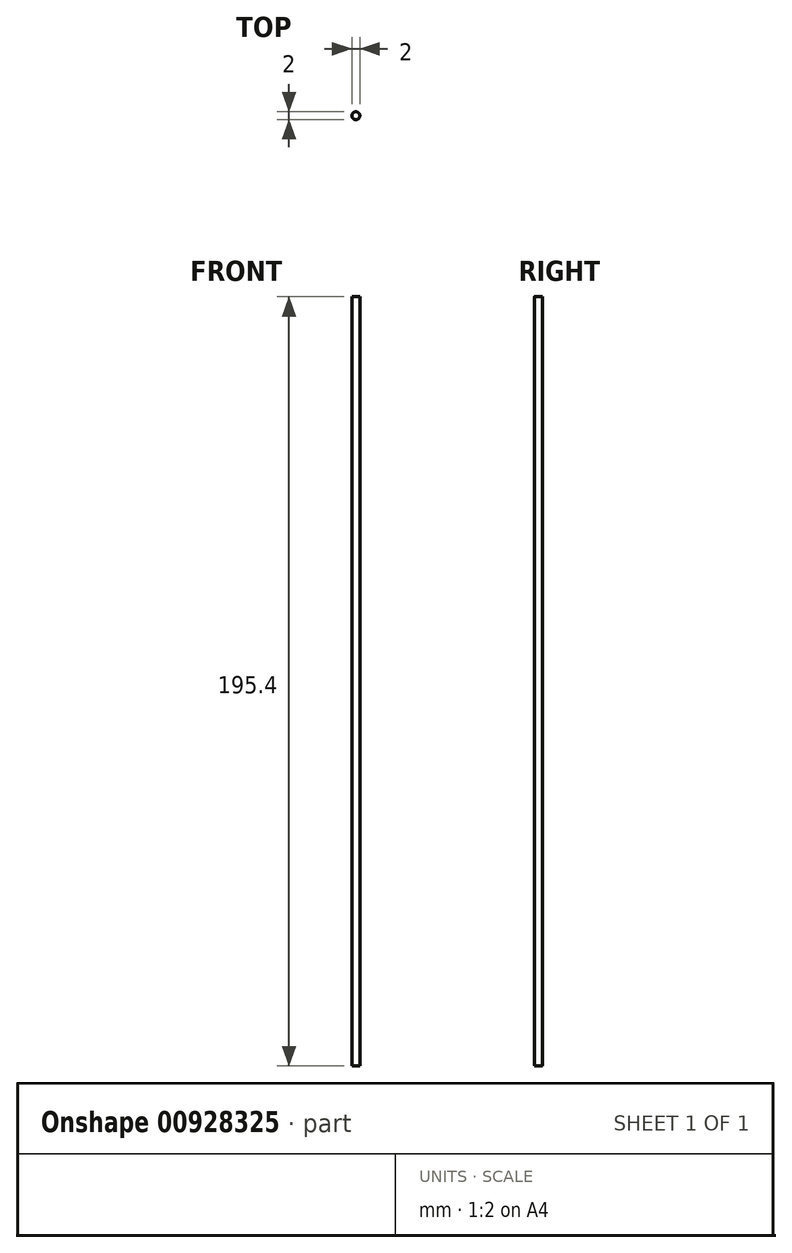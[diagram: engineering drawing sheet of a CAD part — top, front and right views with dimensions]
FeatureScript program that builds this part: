
annotation { "Feature Type Name" : "Feature", "Feature Type Description" : "" }
export const myFeature = defineFeature(function(context is Context, id is Id, definition is map)
    precondition{}
    {
        {
            var Q0;
            Q0=qCreatedBy(makeId("Top.planeOp"),FACE);
            var sketch = newSketch(context, id + "F0", { "sketchPlane" : qUnion([Q0])});
            skCircle(sketch, "E0", {"center": v(0, 0) * mm, "radius": 1 * mm});
            skSolve(sketch);
        }
        {
            var Q0;
            Q0=makeQuery(id+"F0.imprint","IMPRINT",FACE,{"disambiguationData":[TD([[makeQuery(id+"F0.imprint","IMPRINT",EDGE,{"derivedFrom":sQuery(id+"F0.wireOp",EDGE,"E0")}),1.0]])]});
            extrude(context, id + "F1", {"entities" : qUnion([Q0]), "depth" : 195.4 * mm, "offsetDistance" : 25 * mm});
        }
    });
